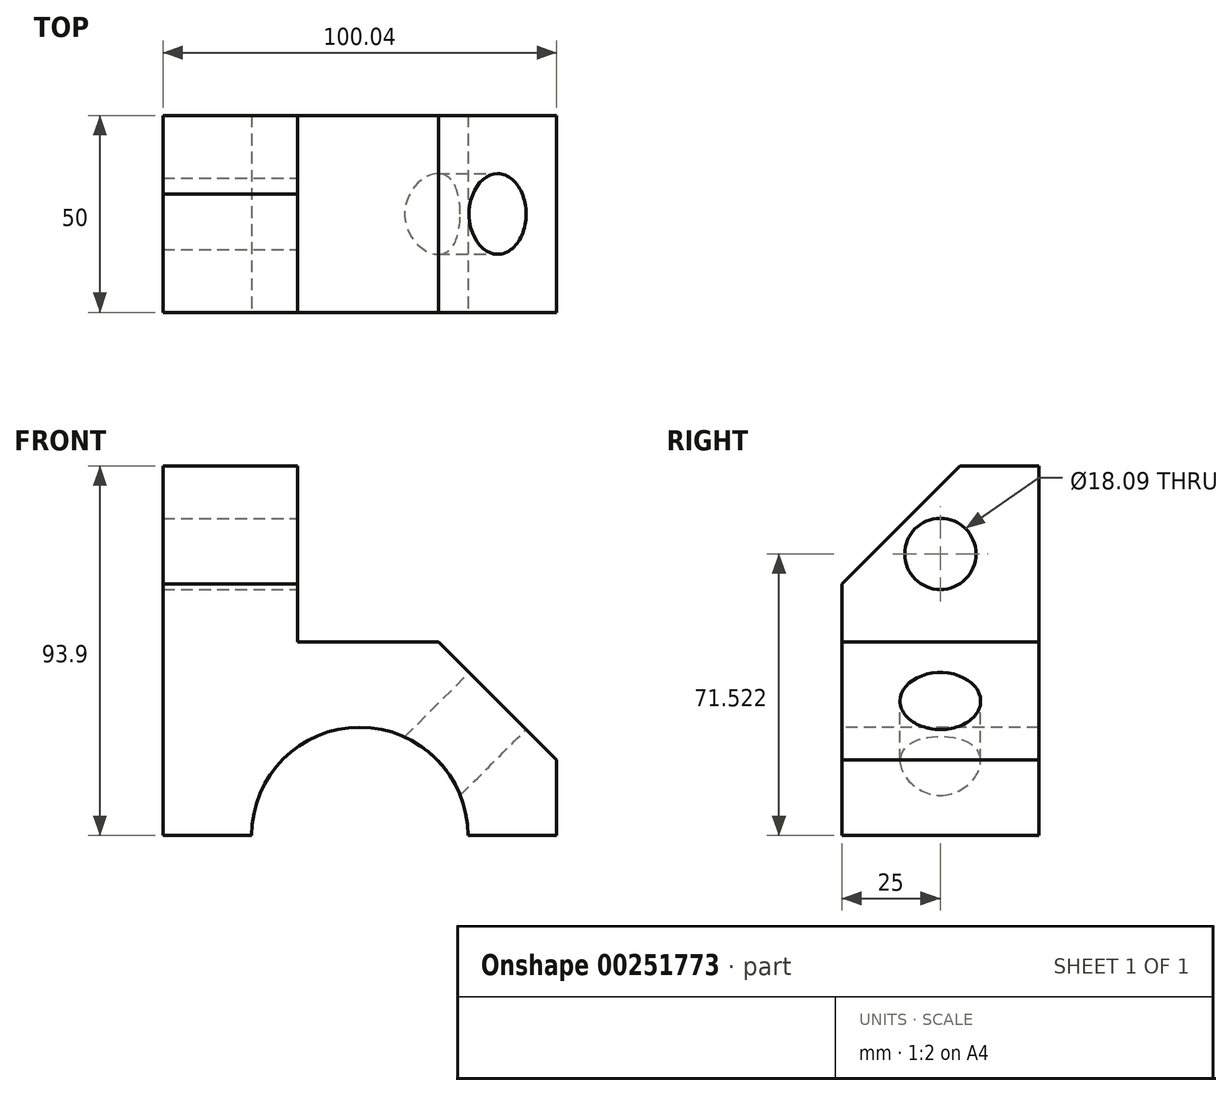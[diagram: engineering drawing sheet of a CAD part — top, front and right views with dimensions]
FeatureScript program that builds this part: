
annotation { "Feature Type Name" : "Feature", "Feature Type Description" : "" }
export const myFeature = defineFeature(function(context is Context, id is Id, definition is map)
    precondition{}
    {
        {
            var Q0;
            Q0=qCreatedBy(makeId("Front.planeOp"),FACE);
            var sketch = newSketch(context, id + "F0", { "sketchPlane" : qUnion([Q0])});
            skLineSegment(sketch, "E0.bottom", {"start": v(-50.02, 24.57) * mm, "end": v(50.02, 24.57) * mm});
            skLineSegment(sketch, "E0.top", {"start": v(-50.02, -24.57) * mm, "end": v(-27.47, -24.57) * mm});
            skLineSegment(sketch, "E0.left", {"start": v(-50.02, 24.57) * mm, "end": v(-50.02, -24.57) * mm});
            skLineSegment(sketch, "E0.right", {"start": v(50.02, 24.57) * mm, "end": v(50.02, -24.57) * mm});
            skPoint(sketch, "E0.middle", {"position": v(0, 0) * mm});
            skLineSegment(sketch, "E1.bottom", {"start": v(-50.02, 24.57) * mm, "end": v(-15.8, 24.57) * mm});
            skLineSegment(sketch, "E1.top", {"start": v(-50.02, 69.33) * mm, "end": v(-15.8, 69.33) * mm});
            skLineSegment(sketch, "E1.left", {"start": v(-50.02, 24.57) * mm, "end": v(-50.02, 69.33) * mm});
            skLineSegment(sketch, "E1.right", {"start": v(-15.8, 24.57) * mm, "end": v(-15.8, 69.33) * mm});
            skArc(sketch, "E2", {"start": v(27.47, -24.57) * mm, "mid": v(0, 2.9) * mm, "end": v(-27.47, -24.57) * mm});
            skLineSegment(sketch, "E3.trimOffspring", {"start": v(27.47, -24.57) * mm, "end": v(50.02, -24.57) * mm});
            skSolve(sketch);
        }
        {
            var Q0;
            Q0 = qSketchRegion(id + "F0", true);
            extrude(context, id + "F1", {"entities" : qUnion([Q0]), "endBound" : BoundingType.SYMMETRIC, "oppositeDirection" : true, "depth" : 50 * mm});
        }
        {
            var Q0;
            Q0=makeQuery(id+"F1.opExtrude","CAP_EDGE",EDGE,{"disambiguationData":[OSD([sQuery(id+"F0.wireOp",EDGE,"E1.top")])],"isStart":true});
            chamfer(context, id + "F2", {"entities" : qUnion([Q0]), "width" : 30 * mm, "tangentPropagation" : true});
        }
        {
            var Q0;
            Q0=makeQuery(id+"F1.opExtrude","SWEPT_EDGE",EDGE,{"disambiguationData":[OSD([sQuery(id+"F0.wireOp",EDGE,"E0.bottom"),sQuery(id+"F0.wireOp",EDGE,"E0.right")])]});
            chamfer(context, id + "F3", {"entities" : qUnion([Q0]), "width" : 30 * mm, "tangentPropagation" : true});
        }
        {
            var Q0;
            Q0=makeQuery(id+"F1.opExtrude","SWEPT_FACE",FACE,{"disambiguationData":[OSD([sQuery(id+"F0.wireOp",EDGE,"E1.right")])]});
            var sketch = newSketch(context, id + "F4", { "sketchPlane" : qUnion([Q0])});
            skCircle(sketch, "E4", {"center": v(0, 46.95) * mm, "radius": 9.05 * mm});
            skPoint(sketch, "E4.centerSnap0", {"position": v(25, 46.95) * mm});
            skSolve(sketch);
        }
        {
            var Q0;
            Q0 = qSketchRegion(id + "F4", true);
            extrude(context, id + "F5", {"entities" : qUnion([Q0]), "operationType" : NewBodyOperationType.REMOVE, "endBound" : BoundingType.THROUGH_ALL, "oppositeDirection" : true, "depth" : 25 * mm});
        }
        {
            var Q0;
            Q0=makeQuery(id+"F3.opChamfer","BLEND_FACE",FACE,{"disambiguationData":[OSD([sQuery(id+"F0.wireOp",EDGE,"E0.bottom"),sQuery(id+"F0.wireOp",EDGE,"E0.right")])]});
            var sketch = newSketch(context, id + "F6", { "sketchPlane" : qUnion([Q0])});
            skCircle(sketch, "E5", {"center": v(0, -18) * mm, "radius": 10.23 * mm});
            skPoint(sketch, "E5.centerSnap0", {"position": v(25, -18) * mm});
            skSolve(sketch);
        }
        {
            var Q0;
            Q0 = qSketchRegion(id + "F6", true);
            extrude(context, id + "F7", {"entities" : qUnion([Q0]), "operationType" : NewBodyOperationType.REMOVE, "endBound" : BoundingType.THROUGH_ALL, "oppositeDirection" : true, "depth" : 25 * mm});
        }
    });
